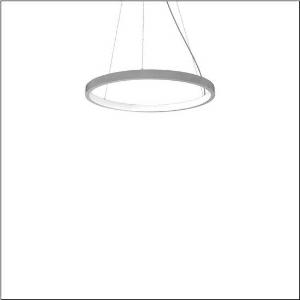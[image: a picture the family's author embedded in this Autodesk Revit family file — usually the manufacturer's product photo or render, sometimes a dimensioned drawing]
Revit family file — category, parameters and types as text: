
# Revit family: silica_r__21_ring-i_5pjbi2d1204a_a024
name_source: partatom
category: Lighting Fixtures
units: mm (PartAtom-declared; Revit-internal decimal feet)

## family parameters
Cut with Voids When Loaded = No
Host = Face
Light Source = No
Part Type = Normal
Room Calculation Point = No
Round Connector Dimension = Use Diameter
Shared = No

## types (1)
- Silica® 21 Ring-I (1 x LED, 4800 lm, 80 W, 3000K)
    Apparent Load = 80 VA
    CIE Flux Codes = 22 48 76 50 101
    Color Rendering = 80
    Color Temperature = 3000K
    Default Elevation = 1800 mm
    Description = Silica® 21 Ring-I, suspended luminaire, of PMMA, frosted, light emission: inner ring side luminous distribution, primary light characteristic: symmetric, installation type: suspended mounting, LED, rated luminous flux: 4.800lm, luminous efficacy: 60lm/W, light colour: 830, colour temperature: 3000K, control gear: DALI 2, with terminal, 5-pole, mains connection: 230V, AC/DC, 0/50..60Hz, rated input power: 80W, housing, of extruded aluminium section, metallic grey (RAL 9006), diameter: 805mm, ceiling canopy, metallic grey (RAL 9006), protection rating (lamp compartment): IP40, insulation class (complete): insulation class I (protective earthing), certification: CE, impact resistance: IK02, permissible operating ambient temperature: 0..+35°C, packaging unit: 1 piece
    Height = 48 mm  [stored 0.15748 ft]
    Lamp = 1 x LED
    Lamp Light Flux = 4800 lm
    Lamp Power = 80 W
    Lamp count = 1
    Length = 805 mm
    Luminous efficacy = 60 lm/W
    Manufacturer = Siteco
    ModVariant = No
    Model = 5PJBI2D1204A
    Mounting Place = Ceiling
    Mounting Type = Pendant
    Number of Poles = 1
    OnlyDefault = Yes
    Power Factor = 1
    Product Name = Silica® 21 Ring-I
    Product group = suspended luminaire
    ProductGroupID = 905
    Protection Class = Protection class I
    Protection Degree = IP 40
    RLX_Detail_Level = 1
    RLX_Emergency_Light_Flux = 0 lm
    RLX_Emergency_Type = 0
    RLX_Emergency_Type_DB = No
    RlxData = <blob elided: 13117 chars, md5=e6dffa1d>
    Socket = socket
    Standby Power = 0 W
    System Light Flux = 4800 lm
    System Power = 80 W
    Type Comments = Product without accessories
    Type Image = l_1251752.jpg
    URL = http://relux.com
    VarID = ---
    Voltage = 0 V
    Weight = 0.00 kg
    Width = 0 mm  [stored 0 ft]

note: [stored X ft] marks values corroborated as IEEE doubles in the binary element streams (Revit-internal decimal feet)

## geometry (parser evidence)
native form markers: Sweep x9
no freeform markers — native parametric forms only
